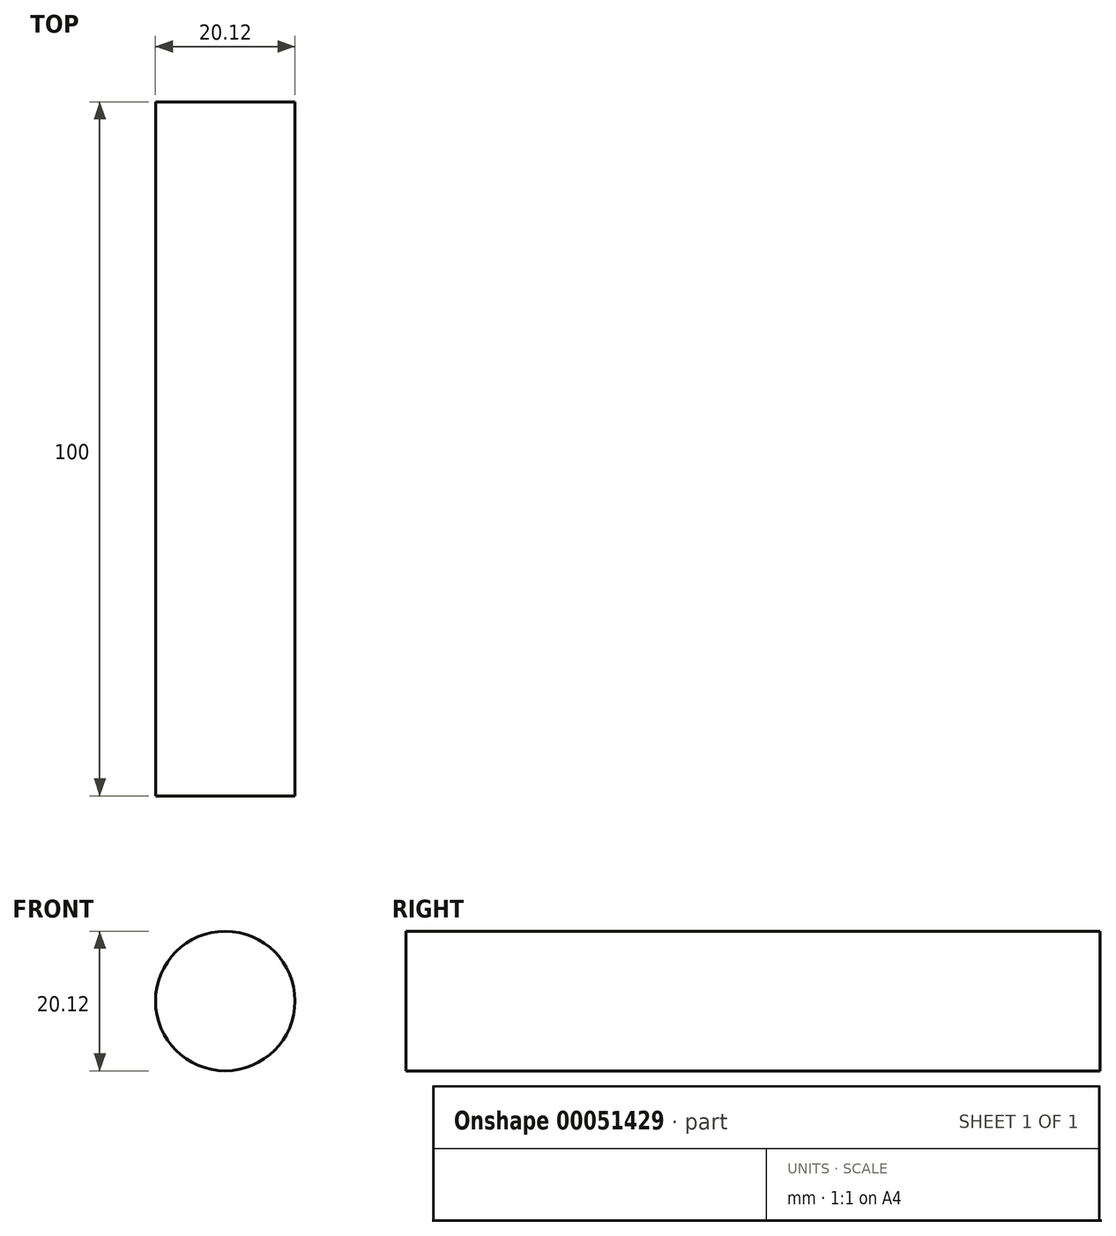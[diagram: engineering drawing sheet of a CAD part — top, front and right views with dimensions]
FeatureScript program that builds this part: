
annotation { "Feature Type Name" : "Feature", "Feature Type Description" : "" }
export const myFeature = defineFeature(function(context is Context, id is Id, definition is map)
    precondition{}
    {
        {
            var Q0;
            Q0=qCreatedBy(makeId("Front.planeOp"),FACE);
            var sketch = newSketch(context, id + "F0", { "sketchPlane" : qUnion([Q0])});
            skCircle(sketch, "E0", {"center": v(0, 0) * mm, "radius": 10.05 * mm});
            skSolve(sketch);
        }
        {
            var Q0;
            Q0=makeQuery(id+"F0.imprint","IMPRINT",FACE,{"disambiguationData":[TD([[makeQuery(id+"F0.imprint","IMPRINT",EDGE,{"derivedFrom":sQuery(id+"F0.wireOp",EDGE,"E0")}),1.0]])]});
            var Q1;
            Q1=sQuery(id+"F0.wireOp",EDGE,"E0");
            extrude(context, id + "F1", {"entities" : qUnion([Q0]), "surfaceEntities" : qUnion([Q1]), "depth" : 100 * mm});
        }
    });
